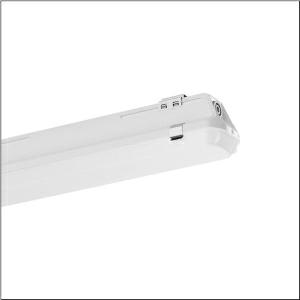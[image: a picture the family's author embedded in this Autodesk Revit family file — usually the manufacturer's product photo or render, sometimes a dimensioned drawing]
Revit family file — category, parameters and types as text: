
# Revit family: monsun_r__11_51fp10ep460h_f2a9
name_source: partatom
category: Lighting Fixtures
units: mm (PartAtom-declared; Revit-internal decimal feet)

## family parameters
Cut with Voids When Loaded = No
Host = Face
Light Source = No
Part Type = Normal
Room Calculation Point = No
Round Connector Dimension = Use Diameter
Shared = No

## types (1)
- --- (1 x LED, 6050 lm, 34.6 W, 4000K)
    Apparent Load = 35 VA
    CIE Flux Codes = 47 77 93 94 100
    Color Rendering = 80
    Color Temperature = 4000K
    Default Elevation = 1800 mm
    Description = Monsun® 11, damp-proof luminaire, chain hanger, primary optical cover: enclosure, of PMMA, light emission: direct distribution, primary light characteristic: symmetric, installation type: suspended mounting, surface-mounted, horizontal mounting, vertical mounting, LED, rated luminous flux: 6.050lm, luminous efficacy: 175lm/W, light colour: 840, colour temperature: 4000K, control gear: ECG DALI, with terminal, 5-pole, max. 2.5mm², mains connection: 220..240V, AC, 50/60Hz, rated input power: 35W, luminaire housing, of glass-fibre reinforced polyester, uncoated, bright grey, incl. chain hanger, length: 1.590mm, width: 90mm, height: 88mm, clip for enclosure, of stainless steel (V2A), ceiling mounting element, of stainless steel (V2A), chain hanger, of stainless steel (V2A), protection rating (complete): IP66, insulation class (complete): insulation class I (protective earthing), certification: CE, ENEC, VDE, UKCA, protection symbol: D, impact resistance: IK04, permissible operating ambient temperature: -25..+40°C, standard: EN 50419, EN 60598-2-1, no direct snow, no direct sun, no direct rain, for indoor or canopied outdoor use, corresponds to IFS (International Featured Standards) requirements for safety and quality in the food industry, contact your sales advisor before using the luminaires in applications with unclear chemical exposure, large temperature fluctuations or condensation-forming humidity, LABS conformity tested according to VDMA 24364:2018-05, packaging unit: 1 piece
    Height = 89 mm
    Lamp = 1 x LED
    Lamp Light Flux = 6050 lm
    Lamp Power = 34.6 W
    Lamp count = 1
    Length = 1590 mm
    Luminous efficacy = 175 lm/W
    Manufacturer = Siteco
    ModVariant = No
    Model = 51FP10EP460H
    Mounting Place = Ceiling
    Mounting Type = Surface mounted
    Number of Poles = 1
    OnlyDefault = Yes
    Power Factor = 1
    Product Name = Monsun® 11
    Product group = damp-proof luminaire
    ProductGroupID = 300
    Protection Class = Protection class I
    Protection Degree = IP 66
    RLX_Detail_Level = 1
    RLX_Emergency_Light_Flux = 0 lm
    RLX_Emergency_Type = 0
    RLX_Emergency_Type_DB = No
    RlxData = <blob elided: 92205 chars, md5=e55d82ed>
    Socket = socket
    Standby Power = 0 W
    System Light Flux = 6050 lm
    System Power = 35 W
    Type Comments = factory setting: luminous flux: 100 % | dim-lin: 254 | 232 mA
    Type Image = l_1319650.jpg
    URL = http://relux.com
    VarID = @adj_174773
    Voltage = 0 V
    Weight = 0.00 kg
    Width = 90 mm

## geometry (parser evidence)
native form markers: Blend x4, Sweep x13
no freeform markers — native parametric forms only
